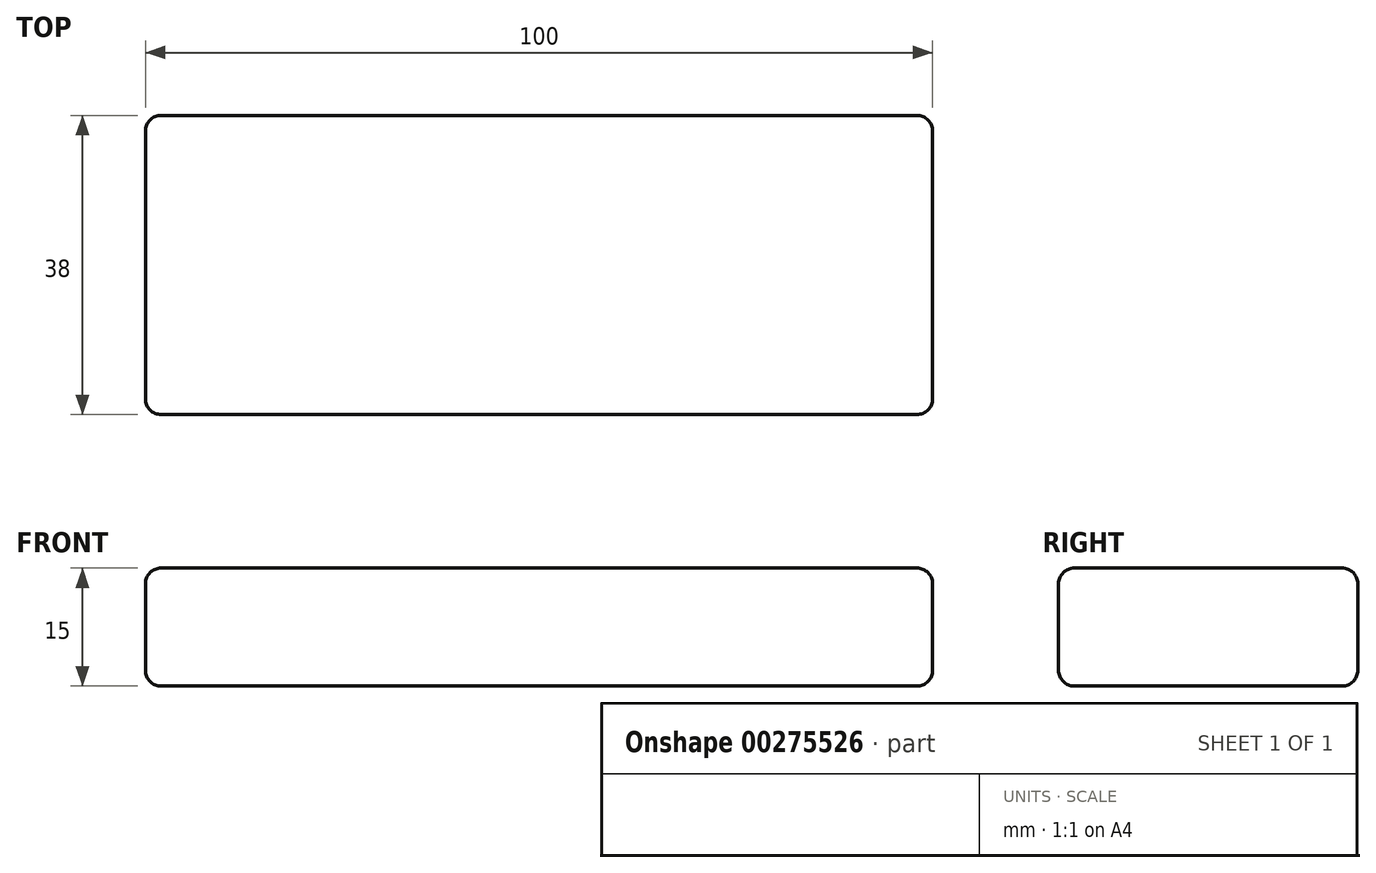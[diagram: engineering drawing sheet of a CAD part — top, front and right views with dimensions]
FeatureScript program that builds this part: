
annotation { "Feature Type Name" : "Feature", "Feature Type Description" : "" }
export const myFeature = defineFeature(function(context is Context, id is Id, definition is map)
    precondition{}
    {
        {
            var Q0;
            Q0=qCreatedBy(makeId("Top.planeOp"),FACE);
            var sketch = newSketch(context, id + "F0", { "sketchPlane" : qUnion([Q0])});
            skLineSegment(sketch, "E0.bottom", {"start": v(50, -19) * mm, "end": v(-50, -19) * mm});
            skLineSegment(sketch, "E0.top", {"start": v(50, 19) * mm, "end": v(-50, 19) * mm});
            skLineSegment(sketch, "E0.left", {"start": v(50, -19) * mm, "end": v(50, 19) * mm});
            skLineSegment(sketch, "E0.right", {"start": v(-50, -19) * mm, "end": v(-50, 19) * mm});
            skPoint(sketch, "E0.middle", {"position": v(0, 0) * mm});
            skSolve(sketch);
        }
        {
            var Q0;
            Q0 = qSketchRegion(id + "F0", true);
            extrude(context, id + "F1", {"entities" : qUnion([Q0]), "depth" : 15 * mm});
        }
        {
            var Q0;
            Q0=makeQuery(id+"F1.opExtrude","CAP_FACE",FACE,{"disambiguationData":[OSD([sQuery(id+"F0.wireOp",EDGE,"E0.bottom"),sQuery(id+"F0.wireOp",EDGE,"E0.top"),sQuery(id+"F0.wireOp",EDGE,"E0.left"),sQuery(id+"F0.wireOp",EDGE,"E0.right")])],"isStart":false});
            var Q1;
            Q1=makeQuery(id+"F1.opExtrude","CAP_FACE",FACE,{"disambiguationData":[OSD([sQuery(id+"F0.wireOp",EDGE,"E0.bottom"),sQuery(id+"F0.wireOp",EDGE,"E0.top"),sQuery(id+"F0.wireOp",EDGE,"E0.left"),sQuery(id+"F0.wireOp",EDGE,"E0.right")])],"isStart":true});
            var Q2;
            Q2=makeQuery(id+"F1.opExtrude","SWEPT_EDGE",EDGE,{"disambiguationData":[OSD([sQuery(id+"F0.wireOp",EDGE,"E0.top"),sQuery(id+"F0.wireOp",EDGE,"E0.right")])]});
            var Q3;
            Q3=makeQuery(id+"F1.opExtrude","SWEPT_EDGE",EDGE,{"disambiguationData":[OSD([sQuery(id+"F0.wireOp",EDGE,"E0.top"),sQuery(id+"F0.wireOp",EDGE,"E0.left")])]});
            var Q4;
            Q4=makeQuery(id+"F1.opExtrude","SWEPT_EDGE",EDGE,{"disambiguationData":[OSD([sQuery(id+"F0.wireOp",EDGE,"E0.bottom"),sQuery(id+"F0.wireOp",EDGE,"E0.left")])]});
            var Q5;
            Q5=makeQuery(id+"F1.opExtrude","SWEPT_EDGE",EDGE,{"disambiguationData":[OSD([sQuery(id+"F0.wireOp",EDGE,"E0.bottom"),sQuery(id+"F0.wireOp",EDGE,"E0.right")])]});
            fillet(context, id + "F2", {"entities" : qUnion([Q0, Q1, Q2, Q3, Q4, Q5]), "radius" : 2 * mm, "tangentPropagation" : true, "allowEdgeOverflow" : false});
        }
    });
